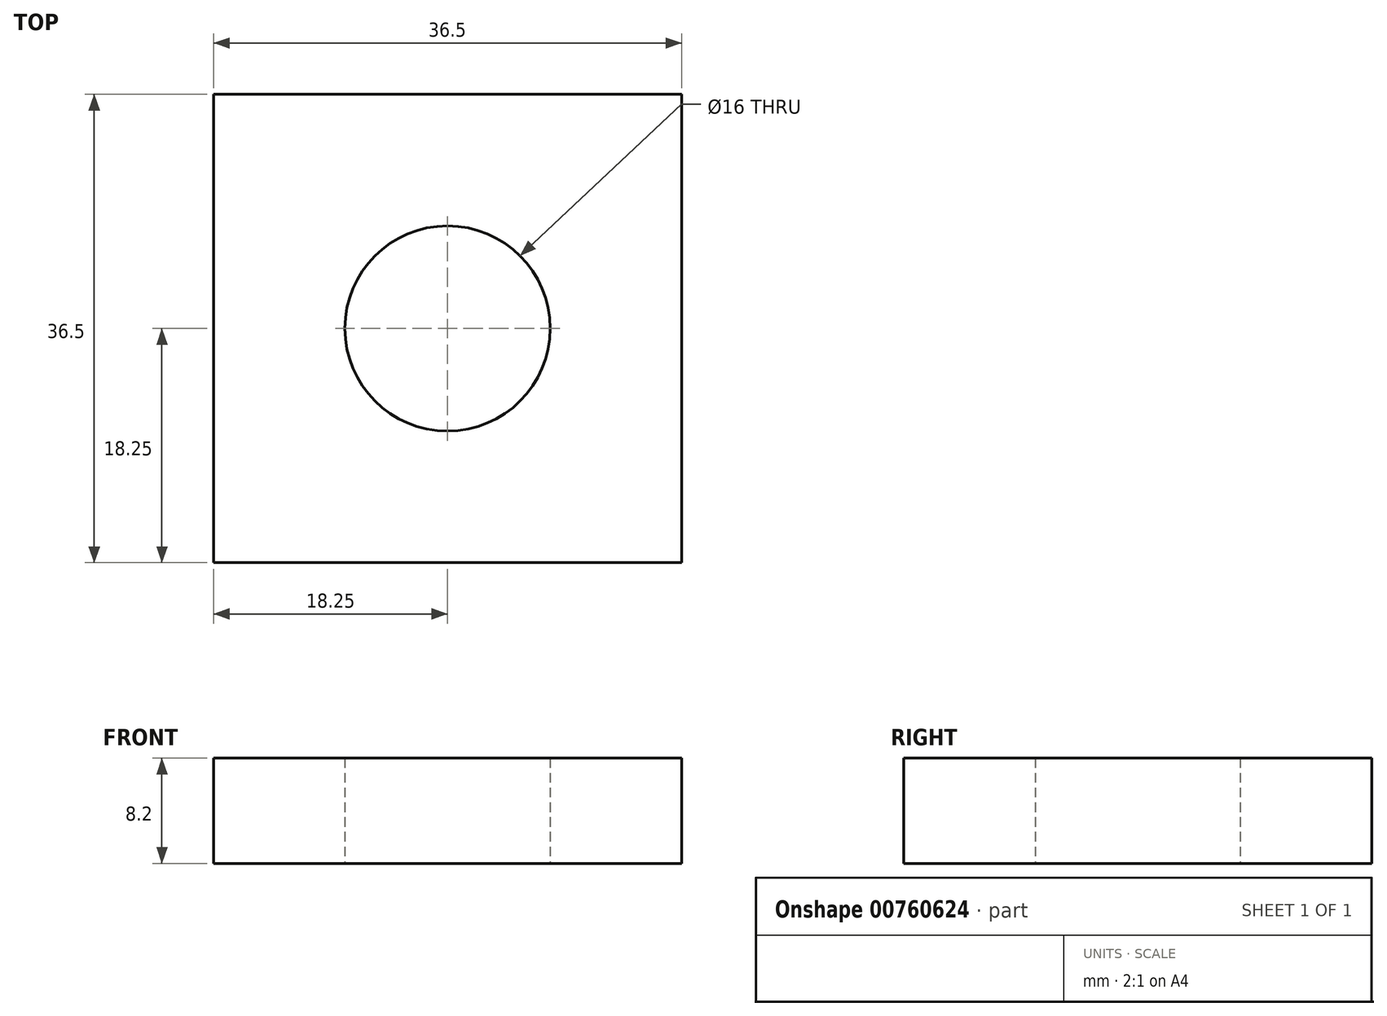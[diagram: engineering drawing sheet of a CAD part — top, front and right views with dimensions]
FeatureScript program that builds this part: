
annotation { "Feature Type Name" : "Feature", "Feature Type Description" : "" }
export const myFeature = defineFeature(function(context is Context, id is Id, definition is map)
    precondition{}
    {
        {
            var Q0;
            Q0=qCreatedBy(makeId("Top.planeOp"),FACE);
            var sketch = newSketch(context, id + "F0", { "sketchPlane" : qUnion([Q0])});
            skCircle(sketch, "E0", {"center": v(0, 0) * mm, "radius": 8 * mm});
            skLineSegment(sketch, "E1.bottom", {"start": v(-18.25, 18.25) * mm, "end": v(18.25, 18.25) * mm});
            skLineSegment(sketch, "E1.top", {"start": v(-18.25, -18.25) * mm, "end": v(18.25, -18.25) * mm});
            skLineSegment(sketch, "E1.left", {"start": v(-18.25, 18.25) * mm, "end": v(-18.25, -18.25) * mm});
            skLineSegment(sketch, "E1.right", {"start": v(18.25, 18.25) * mm, "end": v(18.25, -18.25) * mm});
            skSolve(sketch);
        }
        {
            var Q0;
            Q0 = qSketchRegion(id + "F0", true);
            extrude(context, id + "F1", {"entities" : qUnion([Q0]), "depth" : 8.2 * mm, "offsetDistance" : 25 * mm});
        }
    });
